# Revit family: Sanitary_Showers_AXOR_48655XXX-AXOR-One-Bidette-hand-shower-1jet-round-for-cold-water-with-shower-holder_NEW
name_source: partatom
category: Plumbing Fixtures
units: mm (PartAtom-declared; Revit-internal decimal feet)

## family parameters
Cut with Voids When Loaded = Yes
Host = Face
Maintain Annotation Orientation = No
OmniClass Number = 23.31.17.00
OmniClass Title = Showers
Part Type = Normal
Room Calculation Point = No
Round Connector Dimension = Use Diameter
Shared = No

## types (1)
- 48655XXX AXOR One Bidette hand shower 1jet round for cold water with shower holder and hose 1.25 m
    Connector Description = Cold Water Inlet 12.7mm
    Default Elevation = 1219 mm
    Description = AXOR One Bidette hand shower 1jet round for cold water with shower holder and hose 1.25 m
    Diameter = 13 mm  [stored 0.0426509 ft]
    Manufacturer = AXOR
    Material 1 = AXOR - Metal - 000 Chrome
    Model = 48655XXX
    Product Page URL = https://www.axor-design.com
    Product data url = https://bimobject.com
    URL = https://www.axor-design.com
    Version = 1

note: [stored X ft] marks values corroborated as IEEE doubles in the binary element streams (Revit-internal decimal feet)

## geometry (parser evidence)
native form markers: Sweep x1
no freeform markers — native parametric forms only
